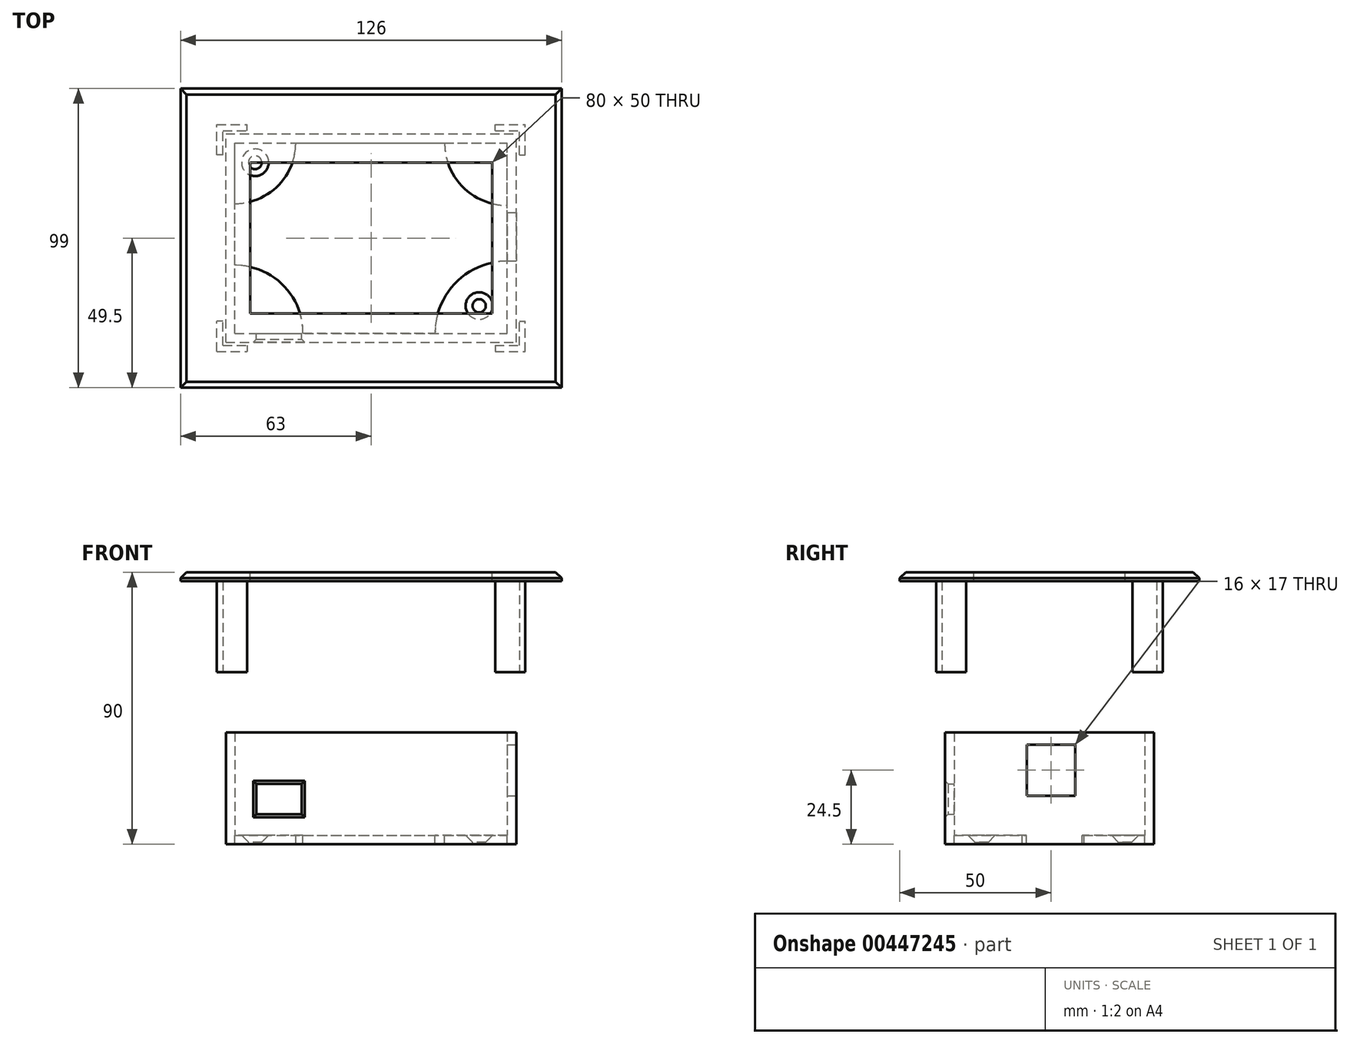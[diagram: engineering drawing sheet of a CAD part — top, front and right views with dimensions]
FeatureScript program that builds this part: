
annotation { "Feature Type Name" : "Feature", "Feature Type Description" : "" }
export const myFeature = defineFeature(function(context is Context, id is Id, definition is map)
    precondition{}
    {
        {
            var Q0;
            Q0=qCreatedBy(makeId("Top.planeOp"),FACE);
            var sketch = newSketch(context, id + "F0", { "sketchPlane" : qUnion([Q0])});
            skLineSegment(sketch, "E0.bottom", {"start": v(0, 0) * mm, "end": v(96, 0) * mm});
            skLineSegment(sketch, "E0.top", {"start": v(0, 69) * mm, "end": v(96, 69) * mm});
            skLineSegment(sketch, "E0.left", {"start": v(0, 0) * mm, "end": v(0, 69) * mm});
            skLineSegment(sketch, "E0.right", {"start": v(96, 0) * mm, "end": v(96, 69) * mm});
            skSolve(sketch);
        }
        {
            var Q0;
            Q0=qSketchRegion(id+"F0",true);
            extrude(context, id + "F1", {"entities" : qUnion([Q0]), "depth" : 37 * mm});
        }
        {
            var Q0;
            Q0=makeQuery(id+"F1.opExtrude","CAP_FACE",FACE,{"disambiguationData":[OSD([sQuery(id+"F0.wireOp",EDGE,"E0.bottom"),sQuery(id+"F0.wireOp",EDGE,"E0.top"),sQuery(id+"F0.wireOp",EDGE,"E0.left"),sQuery(id+"F0.wireOp",EDGE,"E0.right")])],"isStart":false});
            shell(context, id + "F2", {"entities" : qUnion([Q0]), "thickness" : 3 * mm});
        }
        {
            var Q0;
            Q0=makeQuery(id+"F2.opShell","OFFSET_FACE",FACE,{"disambiguationData":[OSD([sQuery(id+"F0.wireOp",EDGE,"E0.bottom"),sQuery(id+"F0.wireOp",EDGE,"E0.top"),sQuery(id+"F0.wireOp",EDGE,"E0.left"),sQuery(id+"F0.wireOp",EDGE,"E0.right")])]});
            var sketch = newSketch(context, id + "F3", { "sketchPlane" : qUnion([Q0])});
            skPoint(sketch, "E1", {"position": v(9.66, 59.5) * mm});
            skPoint(sketch, "E2", {"position": v(83.73, 12.1) * mm});
            skSolve(sketch);
        }
        {
            var Q0;
            Q0=sQuery(id+"F3.wireOp",VERTEX,"E1");
            var Q1;
            Q1=makeQuery(id+"F1.opExtrude","SWEPT_BODY",BODY,{"disambiguationData":[OSD([sQuery(id+"F0.wireOp",EDGE,"E0.bottom"),sQuery(id+"F0.wireOp",EDGE,"E0.top"),sQuery(id+"F0.wireOp",EDGE,"E0.left"),sQuery(id+"F0.wireOp",EDGE,"E0.right")])]});
            hole(context, id + "F4", {"style" : HoleStyle.C_SINK, "endStyle" : HoleEndStyle.THROUGH, "standardTappedOrClearance" : lookupTablePath({ "standard" : "ISO", "fit" : "Normal", "size" : "M4", "type" : "Clearance" }), "standardBlindInLast" : lookupTablePath({ "fit" : "Standard", "standard" : "ISO", "size" : "M4", "type" : "Clearance" }), "holeDiameter" : 4.4 * mm, "cSinkDiameter" : 8.96 * mm, "cSinkAngle" : 90 * degree, "isTappedThrough" : true, "tappedDepth" : 12 * mm, "tapClearance" : 3, "locations" : qUnion([Q0]), "scope" : qUnion([Q1])});
        }
        {
            var Q0;
            Q0=sQuery(id+"F3.wireOp",VERTEX,"E2");
            var Q1;
            Q1=makeQuery(id+"F1.opExtrude","SWEPT_BODY",BODY,{"disambiguationData":[OSD([sQuery(id+"F0.wireOp",EDGE,"E0.bottom"),sQuery(id+"F0.wireOp",EDGE,"E0.top"),sQuery(id+"F0.wireOp",EDGE,"E0.left"),sQuery(id+"F0.wireOp",EDGE,"E0.right")])]});
            hole(context, id + "F5", {"style" : HoleStyle.C_SINK, "endStyle" : HoleEndStyle.THROUGH, "standardTappedOrClearance" : lookupTablePath({ "standard" : "ISO", "fit" : "Normal", "size" : "M4", "type" : "Clearance" }), "standardBlindInLast" : lookupTablePath({ "fit" : "Standard", "standard" : "ISO", "size" : "M4", "type" : "Clearance" }), "holeDiameter" : 4.4 * mm, "cSinkDiameter" : 8.96 * mm, "cSinkAngle" : 90 * degree, "isTappedThrough" : true, "tappedDepth" : 12 * mm, "tapClearance" : 3, "locations" : qUnion([Q0]), "scope" : qUnion([Q1])});
        }
        {
            var Q0;
            Q0=makeQuery(id+"Fv2Lp8H76RmDUAu_1.boolean.opBoolean","MERGE",FACE,{"derivedFrom":[makeQuery(id+"F2.opShell","OFFSET_FACE",FACE,{"disambiguationData":[OSD([sQuery(id+"F0.wireOp",EDGE,"E0.bottom")])]}),makeQuery(id+"Fv2Lp8H76RmDUAu_1.opExtrude","SWEPT_FACE",FACE,{"disambiguationData":[OSD([sQuery(id+"FU4CP0wZnbrBb0s_1.wireOp",EDGE,"30jitwlD-jqMr-7I8g-f0zv-U9qNJRmIhCNw.top")])]})]});
            var sketch = newSketch(context, id + "F6", { "sketchPlane" : qUnion([Q0])});
            skLineSegment(sketch, "E3.bottom", {"start": v(-10, 10) * mm, "end": v(-25, 10) * mm});
            skLineSegment(sketch, "E3.top", {"start": v(-10, 20) * mm, "end": v(-25, 20) * mm});
            skLineSegment(sketch, "E3.left", {"start": v(-10, 10) * mm, "end": v(-10, 20) * mm});
            skLineSegment(sketch, "E3.right", {"start": v(-25, 10) * mm, "end": v(-25, 20) * mm});
            skSolve(sketch);
        }
        {
            var Q0;
            Q0=qSketchRegion(id+"F6",true);
            extrude(context, id + "F7", {"entities" : qUnion([Q0]), "operationType" : NewBodyOperationType.REMOVE, "oppositeDirection" : true, "depth" : 4 * mm});
        }
        {
            var Q0;
            Q0=makeQuery(id+"F1.opExtrude","CAP_FACE",FACE,{"disambiguationData":[OSD([sQuery(id+"F0.wireOp",EDGE,"E0.bottom"),sQuery(id+"F0.wireOp",EDGE,"E0.top"),sQuery(id+"F0.wireOp",EDGE,"E0.left"),sQuery(id+"F0.wireOp",EDGE,"E0.right")])],"isStart":false});
            var sketch = newSketch(context, id + "F8", { "sketchPlane" : qUnion([Q0])});
            skLineSegment(sketch, "E4.bottom", {"start": v(-20, 89) * mm, "end": v(124, 89) * mm});
            skLineSegment(sketch, "E4.top", {"start": v(-20, -26) * mm, "end": v(124, -26) * mm});
            skLineSegment(sketch, "E4.left", {"start": v(-20, 89) * mm, "end": v(-20, -26) * mm});
            skLineSegment(sketch, "E4.right", {"start": v(124, 89) * mm, "end": v(124, -26) * mm});
            skSolve(sketch);
        }
        {
            var Q0;
            Q0=makeQuery(id+"F1.opExtrude","SWEPT_FACE",FACE,{"disambiguationData":[OSD([sQuery(id+"F0.wireOp",EDGE,"E0.right")])]});
            var sketch = newSketch(context, id + "F9", { "sketchPlane" : qUnion([Q0])});
            skLineSegment(sketch, "E5.bottom", {"start": v(43, 33) * mm, "end": v(27, 33) * mm});
            skLineSegment(sketch, "E5.top", {"start": v(43, 16) * mm, "end": v(27, 16) * mm});
            skLineSegment(sketch, "E5.left", {"start": v(43, 33) * mm, "end": v(43, 16) * mm});
            skLineSegment(sketch, "E5.right", {"start": v(27, 33) * mm, "end": v(27, 16) * mm});
            skSolve(sketch);
        }
        {
            var Q0;
            Q0=qSketchRegion(id+"F9",true);
            extrude(context, id + "F10", {"entities" : qUnion([Q0]), "operationType" : NewBodyOperationType.REMOVE, "oppositeDirection" : true, "depth" : 3 * mm});
        }
        {
            var Q0;
            Q0=makeQuery(id+"F9.imprint","IMPRINT",FACE,{"disambiguationData":[TD([[makeQuery(id+"F9.imprint","IMPRINT",EDGE,{"derivedFrom":sQuery(id+"F9.wireOp",EDGE,"E5.bottom")}),1.0]])]});
            extrude(context, id + "F11", {"entities" : qUnion([Q0]), "operationType" : NewBodyOperationType.REMOVE, "oppositeDirection" : true, "depth" : 25 * mm});
        }
        {
            var Q0;
            Q0=makeQuery(id+"F7.boolean.opBoolean","INTERSECT",EDGE,{"derivedFrom":[makeQuery(id+"F1.opExtrude","SWEPT_FACE",FACE,{"disambiguationData":[OSD([sQuery(id+"F0.wireOp",EDGE,"E0.bottom")])]}),makeQuery(id+"F7.opExtrude","SWEPT_FACE",FACE,{"disambiguationData":[OSD([sQuery(id+"F6.wireOp",EDGE,"E3.top")])]})]});
            var Q1;
            Q1=makeQuery(id+"F7.boolean.opBoolean","INTERSECT",EDGE,{"derivedFrom":[makeQuery(id+"F1.opExtrude","SWEPT_FACE",FACE,{"disambiguationData":[OSD([sQuery(id+"F0.wireOp",EDGE,"E0.bottom")])]}),makeQuery(id+"F7.opExtrude","SWEPT_FACE",FACE,{"disambiguationData":[OSD([sQuery(id+"F6.wireOp",EDGE,"E3.right")])]})]});
            var Q2;
            Q2=makeQuery(id+"F7.boolean.opBoolean","INTERSECT",EDGE,{"derivedFrom":[makeQuery(id+"F1.opExtrude","SWEPT_FACE",FACE,{"disambiguationData":[OSD([sQuery(id+"F0.wireOp",EDGE,"E0.bottom")])]}),makeQuery(id+"F7.opExtrude","SWEPT_FACE",FACE,{"disambiguationData":[OSD([sQuery(id+"F6.wireOp",EDGE,"E3.bottom")])]})]});
            var Q3;
            Q3=makeQuery(id+"F7.boolean.opBoolean","INTERSECT",EDGE,{"derivedFrom":[makeQuery(id+"F1.opExtrude","SWEPT_FACE",FACE,{"disambiguationData":[OSD([sQuery(id+"F0.wireOp",EDGE,"E0.bottom")])]}),makeQuery(id+"F7.opExtrude","SWEPT_FACE",FACE,{"disambiguationData":[OSD([sQuery(id+"F6.wireOp",EDGE,"E3.left")])]})]});
            var Q4;
            Q4=makeQuery(id+"F10.boolean.opBoolean","COPY",EDGE,{"derivedFrom":makeQuery(id+"F10.opExtrude","CAP_EDGE",EDGE,{"disambiguationData":[OSD([sQuery(id+"F9.wireOp",EDGE,"E5.right")])],"isStart":true})});
            var Q5;
            Q5=makeQuery(id+"F10.boolean.opBoolean","COPY",EDGE,{"derivedFrom":makeQuery(id+"F10.opExtrude","CAP_EDGE",EDGE,{"disambiguationData":[OSD([sQuery(id+"F9.wireOp",EDGE,"E5.top")])],"isStart":true})});
            var Q6;
            Q6=makeQuery(id+"F10.boolean.opBoolean","COPY",EDGE,{"derivedFrom":makeQuery(id+"F10.opExtrude","CAP_EDGE",EDGE,{"disambiguationData":[OSD([sQuery(id+"F9.wireOp",EDGE,"E5.left")])],"isStart":true})});
            var Q7;
            Q7=makeQuery(id+"F10.boolean.opBoolean","COPY",EDGE,{"derivedFrom":makeQuery(id+"F10.opExtrude","CAP_EDGE",EDGE,{"disambiguationData":[OSD([sQuery(id+"F9.wireOp",EDGE,"E5.bottom")])],"isStart":true})});
            chamfer(context, id + "F12", {"entities" : qUnion([Q0, Q1, Q2, Q3, Q4, Q5, Q6, Q7]), "width" : 1 * mm, "tangentPropagation" : true});
        }
        {
            var Q0;
            {var subQ0=sQuery(id+"F0.wireOp",EDGE,"E0.bottom");Q0=makeQuery(id+"F3.imprint","IMPRINT",FACE,{"disambiguationData":[TD([[makeQuery(id+"F3.imprint","IMPRINT",EDGE,{"derivedFrom":makeQuery(id+"F2.opShell","OFFSET_EDGE",EDGE,{"disambiguationData":[OSD([subQ0]),TDD([makeQuery(id+"F1.opExtrude","CAP_EDGE",EDGE,{"disambiguationData":[OSD([subQ0])],"isStart":true})])]})}),1.0]])]});}
            var sketch = newSketch(context, id + "F13", { "sketchPlane" : qUnion([Q0])});
            skLineSegment(sketch, "E6.bottom", {"start": v(3, 3.05) * mm, "end": v(93, 3.05) * mm});
            skLineSegment(sketch, "E6.top", {"start": v(3, 66) * mm, "end": v(93, 66) * mm});
            skLineSegment(sketch, "E6.left", {"start": v(3, 3.05) * mm, "end": v(3, 66) * mm});
            skLineSegment(sketch, "E6.right", {"start": v(93, 3.05) * mm, "end": v(93, 66) * mm});
            skArc(sketch, "E7", {"start": v(25.48, 3.05) * mm, "mid": v(18.9, 18.95) * mm, "end": v(3, 25.54) * mm});
            skArc(sketch, "E8", {"start": v(3, 45.9) * mm, "mid": v(17.2, 51.79) * mm, "end": v(23.09, 66) * mm});
            skArc(sketch, "E9", {"start": v(72.33, 66) * mm, "mid": v(78.39, 51.37) * mm, "end": v(93, 45.31) * mm});
            skArc(sketch, "E10", {"start": v(69.16, 3.05) * mm, "mid": v(76.15, 19.91) * mm, "end": v(93, 26.9) * mm});
            skSolve(sketch);
        }
        {
            var Q0;
            {var subQ6=sQuery(id+"F13.wireOp",EDGE,"E7");var subQ7=sQuery(id+"F13.wireOp",EDGE,"E6.bottom");var subQ8=makeQuery(id+"F13.imprint","INTERSECT",VERTEX,{"derivedFrom":[subQ7,subQ6]});Q0=makeQuery(id+"F13.imprint","IMPRINT",FACE,{"disambiguationData":[TD([[makeQuery(id+"F13.imprint","IMPRINT",EDGE,{"disambiguationData":[TD([[subQ8,-1.0]])],"derivedFrom":subQ7}),1.0]])]});}
            extrude(context, id + "F14", {"entities" : qUnion([Q0]), "operationType" : NewBodyOperationType.REMOVE, "oppositeDirection" : true, "depth" : 25 * mm});
        }
        {
            var Q0;
            Q0=makeQuery(id+"F8.imprint","IMPRINT",FACE,{"disambiguationData":[TD([[makeQuery(id+"F8.imprint","IMPRINT",EDGE,{"derivedFrom":sQuery(id+"F8.wireOp",EDGE,"E4.bottom")}),-1.0]])]});
            cPlane(context, id + "F15", {"entities" : qUnion([Q0]), "cplaneType" : CPlaneType.OFFSET, "offset" : 50 * mm, "width" : 150 * mm, "height" : 150 * mm});
        }
        {
            var Q0;
            Q0=qCreatedBy(id+"F15.planeOp",FACE);
            var sketch = newSketch(context, id + "F16", { "sketchPlane" : qUnion([Q0])});
            skLineSegment(sketch, "E11.bottom", {"start": v(-15, 84) * mm, "end": v(111, 84) * mm});
            skLineSegment(sketch, "E11.top", {"start": v(-15, -15) * mm, "end": v(111, -15) * mm});
            skLineSegment(sketch, "E11.left", {"start": v(-15, 84) * mm, "end": v(-15, -15) * mm});
            skLineSegment(sketch, "E11.right", {"start": v(111, 84) * mm, "end": v(111, -15) * mm});
            skSolve(sketch);
        }
        {
            var Q0;
            Q0 = qSketchRegion(id + "F16", true);
            extrude(context, id + "F17", {"entities" : qUnion([Q0]), "depth" : 3 * mm});
        }
        {
            var Q0;
            Q0=makeQuery(id+"F17.opExtrude","CAP_FACE",FACE,{"disambiguationData":[OSD([sQuery(id+"F16.wireOp",EDGE,"E11.bottom"),sQuery(id+"F16.wireOp",EDGE,"E11.top"),sQuery(id+"F16.wireOp",EDGE,"E11.left"),sQuery(id+"F16.wireOp",EDGE,"E11.right")])],"isStart":false});
            var sketch = newSketch(context, id + "F18", { "sketchPlane" : qUnion([Q0])});
            skLineSegment(sketch, "E12.bottom", {"start": v(8, 59.5) * mm, "end": v(88, 59.5) * mm});
            skLineSegment(sketch, "E12.top", {"start": v(8, 9.5) * mm, "end": v(88, 9.5) * mm});
            skLineSegment(sketch, "E12.left", {"start": v(8, 59.5) * mm, "end": v(8, 9.5) * mm});
            skLineSegment(sketch, "E12.right", {"start": v(88, 59.5) * mm, "end": v(88, 9.5) * mm});
            skSolve(sketch);
        }
        {
            var Q0;
            Q0 = qSketchRegion(id + "F18", true);
            extrude(context, id + "F19", {"entities" : qUnion([Q0]), "operationType" : NewBodyOperationType.REMOVE, "oppositeDirection" : true, "depth" : 5 * mm});
        }
        {
            var Q0;
            Q0=makeQuery(id+"F17.opExtrude","CAP_FACE",FACE,{"disambiguationData":[OSD([sQuery(id+"F16.wireOp",EDGE,"E11.bottom"),sQuery(id+"F16.wireOp",EDGE,"E11.top"),sQuery(id+"F16.wireOp",EDGE,"E11.left"),sQuery(id+"F16.wireOp",EDGE,"E11.right")])],"isStart":true});
            var sketch = newSketch(context, id + "F20", { "sketchPlane" : qUnion([Q0])});
            skLineSegment(sketch, "E13.bottom", {"start": v(-3, 3) * mm, "end": v(99, 3) * mm});
            skLineSegment(sketch, "E13.top", {"start": v(-3, -72) * mm, "end": v(99, -72) * mm});
            skLineSegment(sketch, "E13.left", {"start": v(-3, 3) * mm, "end": v(-3, -72) * mm});
            skLineSegment(sketch, "E13.right", {"start": v(99, 3) * mm, "end": v(99, -72) * mm});
            skSolve(sketch);
        }
        {
            var Q0;
            Q0 = qSketchRegion(id + "F20", true);
            extrude(context, id + "F21", {"entities" : qUnion([Q0]), "operationType" : NewBodyOperationType.ADD, "depth" : 30 * mm});
        }
        {
            var Q0;
            Q0=makeQuery(id+"F21.opExtrude","CAP_FACE",FACE,{"disambiguationData":[OSD([sQuery(id+"F20.wireOp",EDGE,"E13.bottom"),sQuery(id+"F20.wireOp",EDGE,"E13.top"),sQuery(id+"F20.wireOp",EDGE,"E13.left"),sQuery(id+"F20.wireOp",EDGE,"E13.right")])],"isStart":false});
            var sketch = newSketch(context, id + "F22", { "sketchPlane" : qUnion([Q0])});
            skLineSegment(sketch, "E14.bottom", {"start": v(-1, 1) * mm, "end": v(97, 1) * mm});
            skLineSegment(sketch, "E14.top", {"start": v(-1, -70) * mm, "end": v(97, -70) * mm});
            skLineSegment(sketch, "E14.left", {"start": v(-1, 1) * mm, "end": v(-1, -70) * mm});
            skLineSegment(sketch, "E14.right", {"start": v(97, 1) * mm, "end": v(97, -70) * mm});
            skSolve(sketch);
        }
        {
            var Q0;
            Q0 = qSketchRegion(id + "F22", true);
            extrude(context, id + "F23", {"entities" : qUnion([Q0]), "operationType" : NewBodyOperationType.REMOVE, "oppositeDirection" : true, "depth" : 30 * mm});
        }
        {
            var Q0;
            Q0=makeQuery(id+"F17.opExtrude","CAP_EDGE",EDGE,{"disambiguationData":[OSD([sQuery(id+"F16.wireOp",EDGE,"E11.right")])],"isStart":false});
            var Q1;
            Q1=makeQuery(id+"F17.opExtrude","CAP_EDGE",EDGE,{"disambiguationData":[OSD([sQuery(id+"F16.wireOp",EDGE,"E11.top")])],"isStart":false});
            var Q2;
            Q2=makeQuery(id+"F17.opExtrude","CAP_EDGE",EDGE,{"disambiguationData":[OSD([sQuery(id+"F16.wireOp",EDGE,"E11.left")])],"isStart":false});
            var Q3;
            Q3=makeQuery(id+"F17.opExtrude","CAP_EDGE",EDGE,{"disambiguationData":[OSD([sQuery(id+"F16.wireOp",EDGE,"E11.bottom")])],"isStart":false});
            chamfer(context, id + "F24", {"entities" : qUnion([Q0, Q1, Q2, Q3]), "width" : 2 * mm, "tangentPropagation" : true});
        }
        {
            var Q0;
            Q0=makeQuery(id+"F21.opExtrude","SWEPT_FACE",FACE,{"disambiguationData":[OSD([sQuery(id+"F20.wireOp",EDGE,"E13.right")])]});
            var sketch = newSketch(context, id + "F25", { "sketchPlane" : qUnion([Q0])});
            skLineSegment(sketch, "E15.bottom", {"start": v(7, 57) * mm, "end": v(62, 57) * mm});
            skLineSegment(sketch, "E15.top", {"start": v(7, 87) * mm, "end": v(62, 87) * mm});
            skLineSegment(sketch, "E15.left", {"start": v(7, 57) * mm, "end": v(7, 87) * mm});
            skLineSegment(sketch, "E15.right", {"start": v(62, 57) * mm, "end": v(62, 87) * mm});
            skSolve(sketch);
        }
        {
            var Q0;
            Q0 = qSketchRegion(id + "F25", true);
            extrude(context, id + "F26", {"entities" : qUnion([Q0]), "operationType" : NewBodyOperationType.REMOVE, "oppositeDirection" : true, "depth" : 5 * mm});
        }
        {
            var Q0;
            Q0=makeQuery(id+"F21.opExtrude","SWEPT_FACE",FACE,{"disambiguationData":[OSD([sQuery(id+"F20.wireOp",EDGE,"E13.bottom")])]});
            var sketch = newSketch(context, id + "F27", { "sketchPlane" : qUnion([Q0])});
            skLineSegment(sketch, "E16.bottom", {"start": v(7, 57) * mm, "end": v(89, 57) * mm});
            skLineSegment(sketch, "E16.top", {"start": v(7, 87) * mm, "end": v(89, 87) * mm});
            skLineSegment(sketch, "E16.left", {"start": v(7, 57) * mm, "end": v(7, 87) * mm});
            skLineSegment(sketch, "E16.right", {"start": v(89, 57) * mm, "end": v(89, 87) * mm});
            skSolve(sketch);
        }
        {
            var Q0;
            Q0 = qSketchRegion(id + "F27", true);
            extrude(context, id + "F28", {"entities" : qUnion([Q0]), "operationType" : NewBodyOperationType.REMOVE, "oppositeDirection" : true, "depth" : 5 * mm});
        }
        {
            var Q0;
            Q0=makeQuery(id+"F21.opExtrude","SWEPT_FACE",FACE,{"disambiguationData":[OSD([sQuery(id+"F20.wireOp",EDGE,"E13.left")])]});
            var sketch = newSketch(context, id + "F29", { "sketchPlane" : qUnion([Q0])});
            skLineSegment(sketch, "E17.bottom", {"start": v(-62, 57) * mm, "end": v(-7, 57) * mm});
            skLineSegment(sketch, "E17.top", {"start": v(-62, 87) * mm, "end": v(-7, 87) * mm});
            skLineSegment(sketch, "E17.left", {"start": v(-62, 57) * mm, "end": v(-62, 87) * mm});
            skLineSegment(sketch, "E17.right", {"start": v(-7, 57) * mm, "end": v(-7, 87) * mm});
            skSolve(sketch);
        }
        {
            var Q0;
            Q0 = qSketchRegion(id + "F29", true);
            extrude(context, id + "F30", {"entities" : qUnion([Q0]), "operationType" : NewBodyOperationType.REMOVE, "oppositeDirection" : true, "depth" : 5 * mm});
        }
        {
            var Q0;
            Q0=makeQuery(id+"F21.opExtrude","SWEPT_FACE",FACE,{"disambiguationData":[OSD([sQuery(id+"F20.wireOp",EDGE,"E13.top")])]});
            var sketch = newSketch(context, id + "F31", { "sketchPlane" : qUnion([Q0])});
            skLineSegment(sketch, "E18.bottom", {"start": v(-7, 87) * mm, "end": v(-89, 87) * mm});
            skLineSegment(sketch, "E18.top", {"start": v(-7, 57) * mm, "end": v(-89, 57) * mm});
            skLineSegment(sketch, "E18.left", {"start": v(-7, 87) * mm, "end": v(-7, 57) * mm});
            skLineSegment(sketch, "E18.right", {"start": v(-89, 87) * mm, "end": v(-89, 57) * mm});
            skSolve(sketch);
        }
        {
            var Q0;
            Q0 = qSketchRegion(id + "F31", true);
            extrude(context, id + "F32", {"entities" : qUnion([Q0]), "operationType" : NewBodyOperationType.REMOVE, "oppositeDirection" : true, "depth" : 5 * mm});
        }
    });
